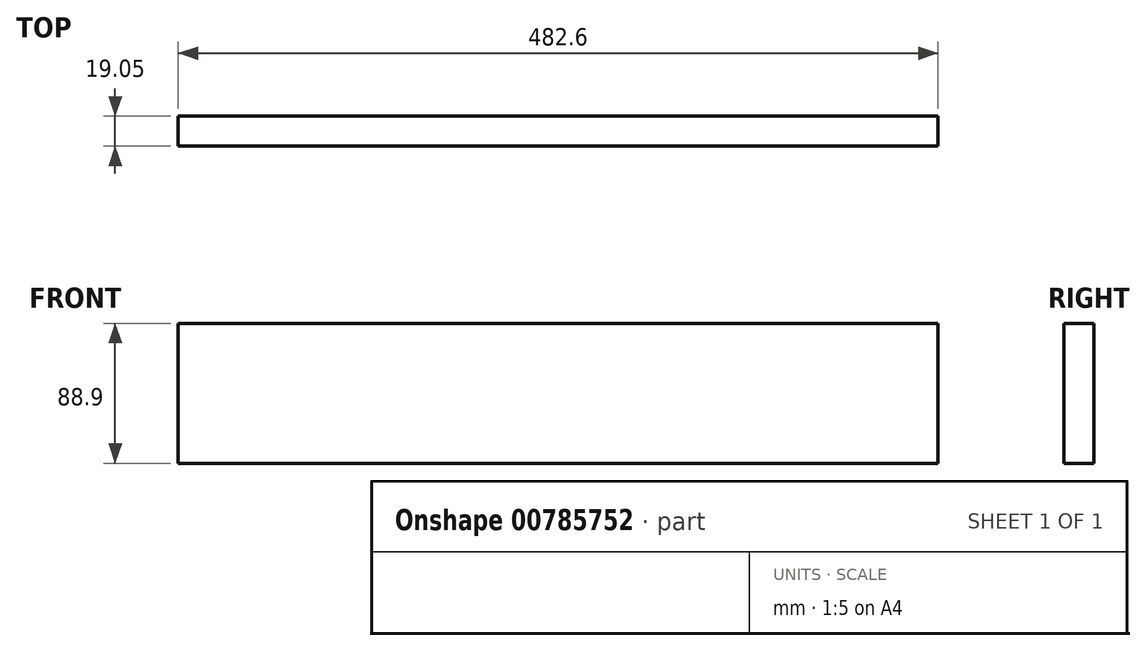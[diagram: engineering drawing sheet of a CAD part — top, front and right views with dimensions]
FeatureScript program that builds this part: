
annotation { "Feature Type Name" : "Feature", "Feature Type Description" : "" }
export const myFeature = defineFeature(function(context is Context, id is Id, definition is map)
    precondition{}
    {
        {
            var Q0;
            Q0=qCreatedBy(makeId("Top.planeOp"),FACE);
            var sketch = newSketch(context, id + "F0", { "sketchPlane" : qUnion([Q0])});
            skLineSegment(sketch, "E0.bottom", {"start": v(-87.29, 22.99) * mm, "end": v(395.31, 22.99) * mm});
            skLineSegment(sketch, "E0.top", {"start": v(-87.29, 3.94) * mm, "end": v(395.31, 3.94) * mm});
            skLineSegment(sketch, "E0.left", {"start": v(-87.29, 22.99) * mm, "end": v(-87.29, 3.94) * mm});
            skLineSegment(sketch, "E0.right", {"start": v(395.31, 22.99) * mm, "end": v(395.31, 3.94) * mm});
            skSolve(sketch);
        }
        {
            var Q0;
            Q0=makeQuery(id+"F0.imprint","IMPRINT",FACE,{"disambiguationData":[TD([[makeQuery(id+"F0.imprint","IMPRINT",EDGE,{"derivedFrom":sQuery(id+"F0.wireOp",EDGE,"E0.bottom")}),-1.0]])]});
            extrude(context, id + "F1", {"entities" : qUnion([Q0]), "oppositeDirection" : true, "depth" : 88.9 * mm, "offsetDistance" : 25.4 * mm});
        }
    });
